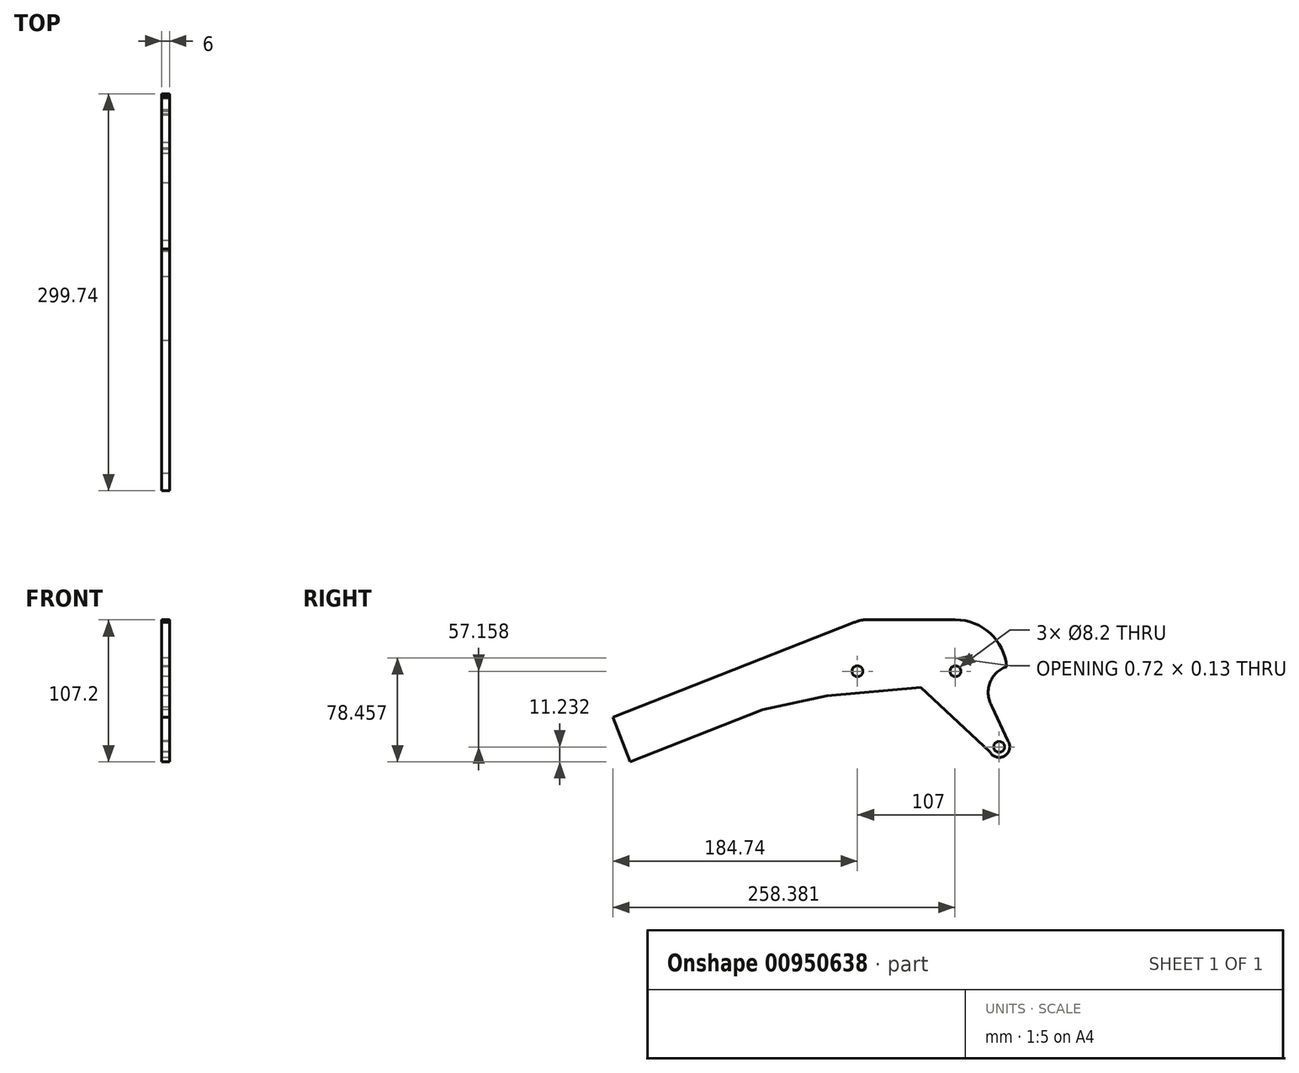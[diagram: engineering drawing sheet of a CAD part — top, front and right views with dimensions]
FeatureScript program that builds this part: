
annotation { "Feature Type Name" : "Feature", "Feature Type Description" : "" }
export const myFeature = defineFeature(function(context is Context, id is Id, definition is map)
    precondition{}
    {
        {
            var Q0;
            Q0=qCreatedBy(makeId("Right.planeOp"),FACE);
            var sketch = newSketch(context, id + "F0", { "sketchPlane" : qUnion([Q0])});
            skCircle(sketch, "E0", {"center": v(0, 0) * mm, "radius": 4.1 * mm});
            skCircle(sketch, "E1", {"center": v(-74, 0) * mm, "radius": 4.1 * mm});
            skLineSegment(sketch, "E2", {"start": v(0, 10) * mm, "end": v(-0.72, 10) * mm});
            skLineSegment(sketch, "E3", {"start": v(-74, 0) * mm, "end": v(0, 0) * mm, "construction": true});
            skLineSegment(sketch, "E4", {"start": v(0, 0) * mm, "end": v(40.21, -69.65) * mm, "construction": true});
            skCircle(sketch, "E5", {"center": v(0, 0) * mm, "radius": 66 * mm, "construction": true});
            skCircle(sketch, "E6", {"center": v(33, -57.16) * mm, "radius": 4.1 * mm});
            skArc(sketch, "E7", {"start": v(25.84, -60.73) * mm, "mid": v(37.05, -64.05) * mm, "end": v(39.6, -52.64) * mm});
            skLineSegment(sketch, "E8", {"start": v(40.7, -54.97) * mm, "end": v(27.67, -27.2) * mm});
            skLineSegment(sketch, "E9", {"start": v(25.84, -60.73) * mm, "end": v(-26.4, -12.26) * mm});
            skArc(sketch, "E10.trimOffspring", {"start": v(0, 10.13) * mm, "mid": v(-0.36, 10.07) * mm, "end": v(-0.72, 10) * mm});
            skPoint(sketch, "E11.end.orphan", {"position": v(0, -13.5) * mm});
            skLineSegment(sketch, "E12.top", {"start": v(0, 38.8) * mm, "end": v(-67.64, 38.8) * mm});
            skLineSegment(sketch, "E12.left", {"start": v(0, 10) * mm, "end": v(0, 38.8) * mm});
            skLineSegment(sketch, "E13", {"start": v(-25.4, -12.26) * mm, "end": v(-97.03, -18.6) * mm});
            skArc(sketch, "E14.trimOffspring", {"start": v(27.67, -27.2) * mm, "mid": v(27.78, -27.1) * mm, "end": v(27.88, -27) * mm});
            skArc(sketch, "E15.trimOffspring", {"start": v(38.65, 3.48) * mm, "mid": v(26.18, 28.64) * mm, "end": v(0, 38.8) * mm});
            skArc(sketch, "E16.trimOffspring", {"start": v(38.65, 3.48) * mm, "mid": v(25.87, -9.14) * mm, "end": v(27.88, -27) * mm});
            skPoint(sketch, "E17.visualSharp", {"position": v(-72.15, 38.8) * mm});
            skArc(sketch, "E17.filletArc", {"start": v(-67.64, 38.8) * mm, "mid": v(-72.04, 38.32) * mm, "end": v(-76.22, 36.87) * mm});
            skLineSegment(sketch, "E18", {"start": v(38.65, 3.48) * mm, "end": v(-258.8, 0) * mm, "construction": true});
            skLineSegment(sketch, "E19", {"start": v(-258.8, 0) * mm, "end": v(-339.16, -0.94) * mm, "construction": true});
            skCircle(sketch, "E20", {"center": v(-74, 0) * mm, "radius": 188 * mm, "construction": true});
            skCircle(sketch, "E21", {"center": v(-262, -0.04) * mm, "radius": 35 * mm, "construction": true});
            skLineSegment(sketch, "E22", {"start": v(-76.22, 36.87) * mm, "end": v(-258.74, -34.88) * mm});
            skLineSegment(sketch, "E23", {"start": v(-245.56, -68.39) * mm, "end": v(-145.42, -29.02) * mm});
            skLineSegment(sketch, "E24", {"start": v(-258.74, -34.88) * mm, "end": v(-245.56, -68.39) * mm});
            skLineSegment(sketch, "E25", {"start": v(-145.42, -29.02) * mm, "end": v(-97.03, -18.6) * mm});
            skSolve(sketch);
        }
        {
            var Q0;
            Q0 = qSketchRegion(id + "F0", true);
            var Q1;
            Q1=makeQuery(id+"F0.imprint","IMPRINT",FACE,{"disambiguationData":[TD([[makeQuery(id+"F0.imprint","IMPRINT",EDGE,{"derivedFrom":sQuery(id+"F0.wireOp",EDGE,"E0")}),-1.0]])]});
            extrude(context, id + "F1", {"entities" : qUnion([Q0, Q1]), "depth" : 6 * mm, "offsetDistance" : 25 * mm});
        }
    });
